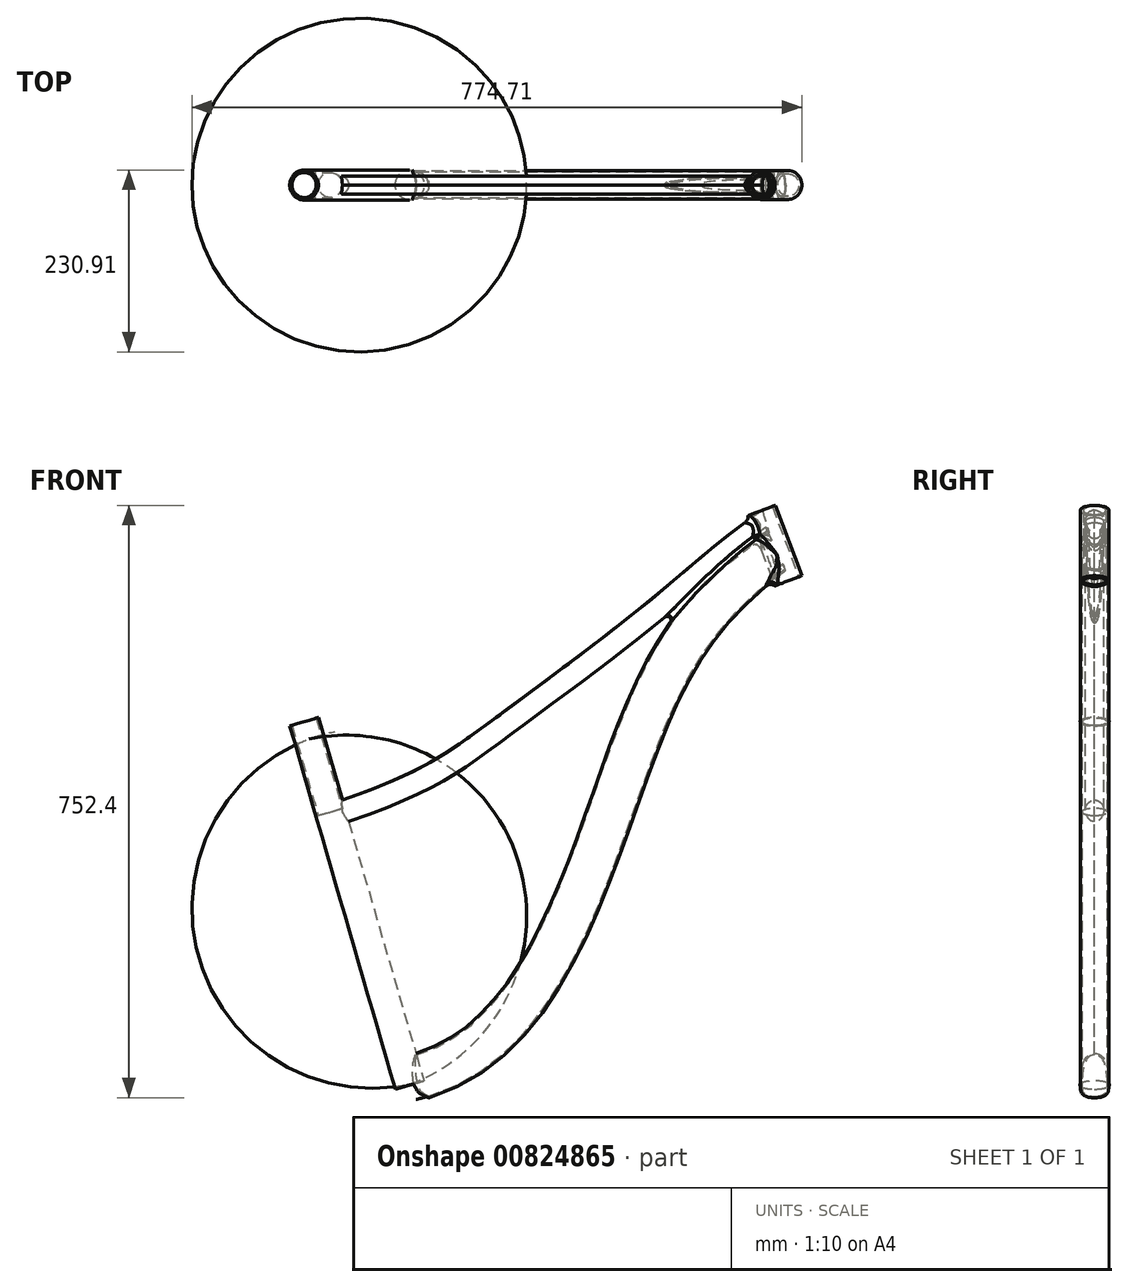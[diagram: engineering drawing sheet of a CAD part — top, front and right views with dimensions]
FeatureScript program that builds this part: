
annotation { "Feature Type Name" : "Feature", "Feature Type Description" : "" }
export const myFeature = defineFeature(function(context is Context, id is Id, definition is map)
    precondition{}
    {
        {
            var Q0;
            Q0=qCreatedBy(makeId("Front.planeOp"),FACE);
            var sketch = newSketch(context, id + "F0", { "sketchPlane" : qUnion([Q0])});
            skLineSegment(sketch, "E0", {"start": v(0, 0) * mm, "end": v(584, 0) * mm, "construction": true});
            skLineSegment(sketch, "E1", {"start": v(0, 0) * mm, "end": v(-584, 0) * mm, "construction": true});
            skCircle(sketch, "E2", {"center": v(-584, 0) * mm, "radius": 311 * mm});
            skCircle(sketch, "E3", {"center": v(584, 0) * mm, "radius": 311 * mm});
            skCircle(sketch, "E4", {"center": v(584, 0) * mm, "radius": 370 * mm});
            skCircle(sketch, "E5", {"center": v(-584, 0) * mm, "radius": 370 * mm});
            skLineSegment(sketch, "E6", {"start": v(-584, -70.94) * mm, "end": v(-139, -70.94) * mm, "construction": true});
            skLineSegment(sketch, "E7", {"start": v(-139, -70.94) * mm, "end": v(-139, 68.19) * mm, "construction": true});
            skLineSegment(sketch, "E8", {"start": v(584, 0) * mm, "end": v(308.44, 729.25) * mm, "construction": true});
            skLineSegment(sketch, "E9", {"start": v(-139, 0) * mm, "end": v(-321.56, 628.38) * mm, "construction": true});
            skPoint(sketch, "E10", {"position": v(-272.92, 460.94) * mm});
            skLineSegment(sketch, "E11", {"start": v(421.54, -332.43) * mm, "end": v(-746.46, -332.43) * mm, "construction": true});
            skPoint(sketch, "E12", {"position": v(329.44, 673.67) * mm});
            skFitSpline(sketch, "E13", {"points": [v(-139, 0) * mm, v(57.4, 180.26) * mm, v(171.31, 471.97) * mm, v(329.44, 673.67) * mm], "startDerivative": vector(868.1, 183) * mm, "endDerivative": vector(779.1, 577.52) * mm});
            skPoint(sketch, "E14", {"position": v(541.58, 112.25) * mm});
            skCircle(sketch, "E15", {"center": v(541.58, 112.25) * mm, "radius": 370 * mm, "construction": true});
            skCircle(sketch, "E16", {"center": v(541.58, 112.25) * mm, "radius": 311 * mm, "construction": true});
            skLineSegment(sketch, "E17", {"start": v(61.85, -332.43) * mm, "end": v(61.85, 447.57) * mm, "construction": true});
            skLineSegment(sketch, "E18", {"start": v(61.85, 447.57) * mm, "end": v(-37.41, 447.57) * mm, "construction": true});
            skFitSpline(sketch, "E19", {"points": [v(-239.4, 345.58) * mm, v(-37.41, 447.57) * mm, v(176.43, 610.15) * mm, v(312.12, 719.5) * mm], "startDerivative": vector(1021.83, 342.5) * mm, "endDerivative": vector(568.7, 395.8) * mm});
            skLineSegment(sketch, "E20", {"start": v(308.44, 729.25) * mm, "end": v(325.55, 735.72) * mm});
            skLineSegment(sketch, "E21", {"start": v(325.55, 735.72) * mm, "end": v(356.16, 654.7) * mm});
            skLineSegment(sketch, "E22", {"start": v(321.8, 734.3) * mm, "end": v(352.41, 653.3) * mm});
            skLineSegment(sketch, "E23", {"start": v(356.16, 654.7) * mm, "end": v(359.31, 646.35) * mm});
            skLineSegment(sketch, "E24", {"start": v(352.41, 653.3) * mm, "end": v(355.57, 644.94) * mm});
            skLineSegment(sketch, "E25", {"start": v(359.31, 646.35) * mm, "end": v(355.57, 644.94) * mm});
            skLineSegment(sketch, "E26", {"start": v(-272.92, 460.94) * mm, "end": v(-254.72, 466.23) * mm});
            skLineSegment(sketch, "E27", {"start": v(-254.72, 466.23) * mm, "end": v(-119.27, 0) * mm});
            skLineSegment(sketch, "E28", {"start": v(-257.6, 465.4) * mm, "end": v(-122.4, 0) * mm});
            skLineSegment(sketch, "E29", {"start": v(-139, 0) * mm, "end": v(-272.92, 460.94) * mm});
            skLineSegment(sketch, "E30", {"start": v(-139, 0) * mm, "end": v(-125.59, -46.16) * mm});
            skLineSegment(sketch, "E31", {"start": v(-119.27, 0) * mm, "end": v(-125.38, 21.03) * mm});
            skLineSegment(sketch, "E32", {"start": v(-125.38, 21.03) * mm, "end": v(-105.22, -48.34) * mm});
            skLineSegment(sketch, "E33", {"start": v(-105.22, -48.34) * mm, "end": v(-125.59, -46.16) * mm});
            skSolve(sketch);
        }
        {
            var Q0;
            Q0=qCreatedBy(makeId("Right.planeOp"),FACE);
            cPlane(context, id + "F1", {"entities" : qUnion([Q0]), "cplaneType" : CPlaneType.OFFSET, "offset" : 139 * mm, "oppositeDirection" : true, "width" : 150 * mm, "height" : 150 * mm});
        }
        {
            var Q0;
            Q0=qCreatedBy(id+"F1.planeOp",FACE);
            var sketch = newSketch(context, id + "F2", { "sketchPlane" : qUnion([Q0])});
            skLineSegment(sketch, "E34", {"start": v(0, 0) * mm, "end": v(0, -22.68) * mm});
            skFitSpline(sketch, "E35", {"points": [v(0, -22.68) * mm, v(-9.06, -21.02) * mm, v(-16.68, -13.33) * mm, v(-17.93, -5.33) * mm, v(-18.18, 0) * mm, v(-14.5, 25.97) * mm, v(-7.81, 34.98) * mm, v(0, 37.32) * mm], "startDerivative": vector(-73.75, 0) * mm, "endDerivative": vector(85.37, 4.1) * mm});
            skFitSpline(sketch, "E36.MirrorCS", {"points": [v(0, -22.68) * mm, v(9.06, -21.02) * mm, v(16.68, -13.33) * mm, v(17.93, -5.33) * mm, v(18.18, 0) * mm, v(14.5, 25.97) * mm, v(7.81, 34.98) * mm, v(0, 37.32) * mm], "startDerivative": vector(73.75, 0) * mm, "endDerivative": vector(-85.37, 4.1) * mm});
            skFitSpline(sketch, "E37.0", {"points": [v(0, -20.68) * mm, v(0.74, -20.68) * mm, v(2.17, -20.65) * mm, v(4.14, -20.47) * mm, v(5.67, -20.17) * mm, v(6.85, -19.8) * mm, v(7.73, -19.45) * mm, v(8.6, -19.02) * mm, v(9.78, -18.33) * mm, v(11.23, -17.27) * mm, v(12.54, -16) * mm, v(13.45, -14.9) * mm, v(14.05, -14.06) * mm, v(14.47, -13.33) * mm, v(14.75, -12.75) * mm, v(15, -12.18) * mm, v(15.26, -11.43) * mm, v(15.57, -10.2) * mm, v(15.74, -8.92) * mm, v(15.84, -7.66) * mm, v(15.88, -6.74) * mm, v(15.9, -6) * mm, v(15.93, -5.43) * mm, v(15.95, -4.87) * mm, v(16, -4.23) * mm, v(16.07, -3.29) * mm, v(16.13, -2.37) * mm, v(16.18, -1.27) * mm, v(16.19, -0.29) * mm, v(16.17, 0.91) * mm, v(16.12, 2.77) * mm, v(15.97, 5.52) * mm, v(15.67, 9.28) * mm, v(15.22, 13.27) * mm, v(14.61, 17.3) * mm, v(13.98, 20.48) * mm, v(13.4, 22.83) * mm, v(12.91, 24.45) * mm, v(12.4, 25.9) * mm, v(11.67, 27.62) * mm, v(10.68, 29.4) * mm, v(9.63, 30.77) * mm, v(8.75, 31.7) * mm, v(8.08, 32.3) * mm, v(7.51, 32.75) * mm, v(7.05, 33.09) * mm, v(6.7, 33.32) * mm, v(6.35, 33.55) * mm, v(5.9, 33.82) * mm, v(5.32, 34.13) * mm, v(4.61, 34.45) * mm, v(3.61, 34.8) * mm, v(2.18, 35.14) * mm, v(0.73, 35.28) * mm, v(-0.1, 35.32) * mm]});
            skFitSpline(sketch, "E37.1", {"points": [v(0, -20.68) * mm, v(-0.74, -20.68) * mm, v(-2.17, -20.65) * mm, v(-4.14, -20.47) * mm, v(-5.67, -20.17) * mm, v(-6.85, -19.8) * mm, v(-7.73, -19.45) * mm, v(-8.6, -19.02) * mm, v(-9.78, -18.33) * mm, v(-11.23, -17.27) * mm, v(-12.54, -16) * mm, v(-13.45, -14.9) * mm, v(-14.05, -14.06) * mm, v(-14.47, -13.33) * mm, v(-14.75, -12.75) * mm, v(-15, -12.18) * mm, v(-15.26, -11.43) * mm, v(-15.57, -10.2) * mm, v(-15.74, -8.92) * mm, v(-15.84, -7.66) * mm, v(-15.88, -6.74) * mm, v(-15.9, -6) * mm, v(-15.93, -5.43) * mm, v(-15.95, -4.87) * mm, v(-16, -4.23) * mm, v(-16.07, -3.29) * mm, v(-16.13, -2.37) * mm, v(-16.18, -1.27) * mm, v(-16.19, -0.29) * mm, v(-16.17, 0.91) * mm, v(-16.12, 2.77) * mm, v(-15.97, 5.52) * mm, v(-15.67, 9.28) * mm, v(-15.22, 13.27) * mm, v(-14.61, 17.3) * mm, v(-13.98, 20.48) * mm, v(-13.4, 22.83) * mm, v(-12.91, 24.45) * mm, v(-12.4, 25.9) * mm, v(-11.67, 27.62) * mm, v(-10.68, 29.4) * mm, v(-9.63, 30.77) * mm, v(-8.75, 31.7) * mm, v(-8.08, 32.3) * mm, v(-7.51, 32.75) * mm, v(-7.05, 33.09) * mm, v(-6.7, 33.32) * mm, v(-6.35, 33.55) * mm, v(-5.9, 33.82) * mm, v(-5.32, 34.13) * mm, v(-4.61, 34.45) * mm, v(-3.61, 34.8) * mm, v(-2.18, 35.14) * mm, v(-0.73, 35.28) * mm, v(0.1, 35.32) * mm]});
            skSolve(sketch);
        }
        {
            var Q0;
            Q0=qCreatedBy(makeId("Right.planeOp"),FACE);
            cPlane(context, id + "F3", {"entities" : qUnion([Q0]), "cplaneType" : CPlaneType.OFFSET, "offset" : 239.4 * mm, "oppositeDirection" : true, "width" : 150 * mm, "height" : 150 * mm});
        }
        {
            var Q0;
            Q0=qCreatedBy(id+"F3.planeOp",FACE);
            var sketch = newSketch(context, id + "F4", { "sketchPlane" : qUnion([Q0])});
            skLineSegment(sketch, "E38", {"start": v(0, 345.64) * mm, "end": v(0, 356.28) * mm});
            skFitSpline(sketch, "E39", {"points": [v(0, 356.28) * mm, v(-8.58, 352.29) * mm, v(-11.34, 340.53) * mm, v(-5.74, 328.42) * mm, v(0, 326.28) * mm], "startDerivative": vector(-28.44, 1.13) * mm, "endDerivative": vector(40.47, -0.68) * mm});
            skFitSpline(sketch, "E40.MirrorCS", {"points": [v(0, 356.28) * mm, v(8.58, 352.29) * mm, v(11.34, 340.53) * mm, v(5.74, 328.42) * mm, v(0, 326.28) * mm], "startDerivative": vector(28.44, 1.13) * mm, "endDerivative": vector(-40.47, -0.68) * mm});
            skFitSpline(sketch, "E41.0", {"points": [v(-0.08, 354.28) * mm, v(-0.25, 354.29) * mm, v(-0.7, 354.27) * mm, v(-1.85, 354.07) * mm, v(-3.23, 353.6) * mm, v(-4.61, 352.9) * mm, v(-5.61, 352.26) * mm, v(-6.37, 351.66) * mm, v(-6.92, 351.14) * mm, v(-7.42, 350.6) * mm, v(-7.96, 349.88) * mm, v(-8.51, 348.93) * mm, v(-8.95, 347.88) * mm, v(-9.4, 346.38) * mm, v(-9.67, 344.32) * mm, v(-9.57, 342.07) * mm, v(-9.27, 340.2) * mm, v(-8.82, 338.3) * mm, v(-8.03, 335.94) * mm, v(-6.8, 333.31) * mm, v(-5.67, 331.47) * mm, v(-4.78, 330.3) * mm, v(-4.15, 329.63) * mm, v(-3.6, 329.15) * mm, v(-3.08, 328.83) * mm, v(-2.54, 328.6) * mm, v(-1.88, 328.43) * mm, v(-1.05, 328.32) * mm, v(-0.35, 328.28) * mm, v(0.03, 328.28) * mm]});
            skFitSpline(sketch, "E42.0", {"points": [v(0.08, 354.28) * mm, v(0.25, 354.29) * mm, v(0.7, 354.27) * mm, v(1.85, 354.07) * mm, v(3.23, 353.6) * mm, v(4.61, 352.9) * mm, v(5.61, 352.26) * mm, v(6.37, 351.66) * mm, v(6.92, 351.14) * mm, v(7.42, 350.6) * mm, v(7.96, 349.88) * mm, v(8.51, 348.93) * mm, v(8.95, 347.88) * mm, v(9.4, 346.38) * mm, v(9.67, 344.32) * mm, v(9.57, 342.07) * mm, v(9.27, 340.2) * mm, v(8.82, 338.3) * mm, v(8.03, 335.94) * mm, v(6.8, 333.31) * mm, v(5.67, 331.47) * mm, v(4.78, 330.3) * mm, v(4.15, 329.63) * mm, v(3.6, 329.15) * mm, v(3.08, 328.83) * mm, v(2.54, 328.6) * mm, v(1.88, 328.43) * mm, v(1.05, 328.32) * mm, v(0.35, 328.28) * mm, v(-0.03, 328.28) * mm]});
            skLineSegment(sketch, "E43", {"start": v(-0.57, 354.26) * mm, "end": v(0.57, 354.26) * mm});
            skLineSegment(sketch, "E44", {"start": v(0, 356.28) * mm, "end": v(0, 343.94) * mm});
            skSolve(sketch);
        }
        {
            var Q0;
            Q0=makeQuery(id+"F4.imprint","IMPRINT",FACE,{"disambiguationData":[TD([[makeQuery(id+"F4.imprint","IMPRINT",EDGE,{"derivedFrom":sQuery(id+"F4.wireOp",EDGE,"E39")}),1.0]])]});
            var Q1;
            Q1=sQuery(id+"F0.wireOp",EDGE,"E19");
            sweep(context, id + "F5", {"profiles" : qUnion([Q0]), "path" : qUnion([Q1])});
        }
        {
            var Q0;
            Q0=makeQuery(id+"F2.imprint","IMPRINT",FACE,{"disambiguationData":[TD([[makeQuery(id+"F2.imprint","IMPRINT",EDGE,{"derivedFrom":sQuery(id+"F2.wireOp",EDGE,"E35")}),-1.0]])]});
            var Q1;
            Q1=sQuery(id+"F0.wireOp",EDGE,"E13");
            sweep(context, id + "F6", {"profiles" : qUnion([Q0]), "path" : qUnion([Q1])});
        }
        {
            var Q0;
            {var subQ1=sQuery(id+"F0.wireOp",EDGE,"E21");Q0=makeQuery(id+"F0.imprint","IMPRINT",FACE,{"disambiguationData":[TD([[makeQuery(id+"F0.imprint","IMPRINT",EDGE,{"derivedFrom":subQ1}),-1.0]])]});}
            var Q1;
            Q1=sQuery(id+"F0.wireOp",EDGE,"E8");
            revolve(context, id + "F7", {"operationType" : NewBodyOperationType.ADD, "surfaceOperationType" : NewSurfaceOperationType.NEW, "entities" : qUnion([Q0]), "axis" : qUnion([Q1]), "revolveType" : RevolveType.FULL});
        }
        {
            var Q0;
            Q0=makeQuery(id+"F7.boolean.opBoolean","INTERSECT",EDGE,{"disambiguationData":[OD(0.0)],"derivedFrom":[makeQuery(id+"F5.opSweep","SWEPT_FACE",FACE,{"disambiguationData":[OSD([sQuery(id+"F0.wireOp",EDGE,"E19"),sQuery(id+"F4.wireOp",EDGE,"E39")])]}),makeQuery(id+"F6.opSweep","SWEPT_FACE",FACE,{"disambiguationData":[OSD([sQuery(id+"F0.wireOp",EDGE,"E13"),sQuery(id+"F2.wireOp",EDGE,"E35")])]})]});
            var Q1;
            Q1=makeQuery(id+"F7.boolean.opBoolean","INTERSECT",EDGE,{"disambiguationData":[OD(0.0)],"derivedFrom":[makeQuery(id+"F5.opSweep","SWEPT_FACE",FACE,{"disambiguationData":[OSD([sQuery(id+"F0.wireOp",EDGE,"E19"),sQuery(id+"F4.wireOp",EDGE,"E40.MirrorCS")])]}),makeQuery(id+"F6.opSweep","SWEPT_FACE",FACE,{"disambiguationData":[OSD([sQuery(id+"F0.wireOp",EDGE,"E13"),sQuery(id+"F2.wireOp",EDGE,"E36.MirrorCS")])]})]});
            fillet(context, id + "F8", {"entities" : qUnion([Q0, Q1]), "radius" : 5 * mm, "tangentPropagation" : true, "allowEdgeOverflow" : false});
        }
        {
            var Q0;
            Q0=makeQuery(id+"F7.boolean.opBoolean","INTERSECT",EDGE,{"disambiguationData":[OD(1.0)],"derivedFrom":[makeQuery(id+"F5.opSweep","SWEPT_FACE",FACE,{"disambiguationData":[OSD([sQuery(id+"F0.wireOp",EDGE,"E19"),sQuery(id+"F4.wireOp",EDGE,"E39")])]}),makeQuery(id+"F7.opRevolve","SWEPT_FACE",FACE,{"disambiguationData":[OSD([sQuery(id+"F0.wireOp",EDGE,"E21"),sQuery(id+"F0.wireOp",EDGE,"E23")])]})]});
            var Q1;
            Q1=makeQuery(id+"F7.boolean.opBoolean","INTERSECT",EDGE,{"disambiguationData":[OD(0.0)],"derivedFrom":[makeQuery(id+"F6.opSweep","SWEPT_FACE",FACE,{"disambiguationData":[OSD([sQuery(id+"F0.wireOp",EDGE,"E13"),sQuery(id+"F2.wireOp",EDGE,"E35")])]}),makeQuery(id+"F7.opRevolve","SWEPT_FACE",FACE,{"disambiguationData":[OSD([sQuery(id+"F0.wireOp",EDGE,"E21"),sQuery(id+"F0.wireOp",EDGE,"E23")])]})]});
            var Q2;
            {var subQ0=sQuery(id+"F0.wireOp",EDGE,"E13");var subQ1=makeQuery(id+"F6.opSweep","SWEPT_FACE",FACE,{"disambiguationData":[OSD([subQ0,sQuery(id+"F2.wireOp",EDGE,"E35")])]});var subQ2=sQuery(id+"F0.wireOp",EDGE,"E19");var subQ3=makeQuery(id+"F5.opSweep","SWEPT_FACE",FACE,{"disambiguationData":[OSD([subQ2,sQuery(id+"F4.wireOp",EDGE,"E39")])]});Q2=makeQuery(id+"F8.opFillet","BLEND_EDGE",EDGE,{"blendedFrom":[makeQuery(id+"F7.boolean.opBoolean","INTERSECT",EDGE,{"disambiguationData":[OD(0.0)],"derivedFrom":[subQ3,subQ1]}),makeQuery(id+"F7.boolean.opBoolean","SPLIT",FACE,{"disambiguationData":[TD([makeQuery(id+"F7.opRevolve","SWEPT_FACE",FACE,{"disambiguationData":[OSD([sQuery(id+"F0.wireOp",EDGE,"E20")])]})])],"derivedFrom":makeQuery(id+"F7.opRevolve","SWEPT_FACE",FACE,{"disambiguationData":[OSD([sQuery(id+"F0.wireOp",EDGE,"E21"),sQuery(id+"F0.wireOp",EDGE,"E23")])]})})],"blendedInto":[makeQuery(id+"F7.boolean.opBoolean","SPLIT",FACE,{"disambiguationData":[TD([makeQuery(id+"F7.opRevolve","SWEPT_FACE",FACE,{"disambiguationData":[OSD([sQuery(id+"F0.wireOp",EDGE,"E20")])]})])],"derivedFrom":makeQuery(id+"F7.opRevolve","SWEPT_FACE",FACE,{"disambiguationData":[OSD([sQuery(id+"F0.wireOp",EDGE,"E21"),sQuery(id+"F0.wireOp",EDGE,"E23")])]})})]});}
            var Q3;
            Q3=makeQuery(id+"F7.boolean.opBoolean","INTERSECT",EDGE,{"disambiguationData":[OD(0.0)],"derivedFrom":[makeQuery(id+"F6.opSweep","SWEPT_FACE",FACE,{"disambiguationData":[OSD([sQuery(id+"F0.wireOp",EDGE,"E13"),sQuery(id+"F2.wireOp",EDGE,"E36.MirrorCS")])]}),makeQuery(id+"F7.opRevolve","SWEPT_FACE",FACE,{"disambiguationData":[OSD([sQuery(id+"F0.wireOp",EDGE,"E21"),sQuery(id+"F0.wireOp",EDGE,"E23")])]})]});
            var Q4;
            Q4=makeQuery(id+"F7.boolean.opBoolean","INTERSECT",EDGE,{"disambiguationData":[OD(1.0)],"derivedFrom":[makeQuery(id+"F5.opSweep","SWEPT_FACE",FACE,{"disambiguationData":[OSD([sQuery(id+"F0.wireOp",EDGE,"E19"),sQuery(id+"F4.wireOp",EDGE,"E40.MirrorCS")])]}),makeQuery(id+"F7.opRevolve","SWEPT_FACE",FACE,{"disambiguationData":[OSD([sQuery(id+"F0.wireOp",EDGE,"E21"),sQuery(id+"F0.wireOp",EDGE,"E23")])]})]});
            var Q5;
            {var subQ0=sQuery(id+"F0.wireOp",EDGE,"E13");var subQ1=makeQuery(id+"F6.opSweep","SWEPT_FACE",FACE,{"disambiguationData":[OSD([subQ0,sQuery(id+"F2.wireOp",EDGE,"E36.MirrorCS")])]});var subQ2=sQuery(id+"F0.wireOp",EDGE,"E19");var subQ3=makeQuery(id+"F5.opSweep","SWEPT_FACE",FACE,{"disambiguationData":[OSD([subQ2,sQuery(id+"F4.wireOp",EDGE,"E40.MirrorCS")])]});Q5=makeQuery(id+"F8.opFillet","BLEND_EDGE",EDGE,{"blendedFrom":[makeQuery(id+"F7.boolean.opBoolean","INTERSECT",EDGE,{"disambiguationData":[OD(0.0)],"derivedFrom":[subQ3,subQ1]}),makeQuery(id+"F7.boolean.opBoolean","SPLIT",FACE,{"disambiguationData":[TD([makeQuery(id+"F7.opRevolve","SWEPT_FACE",FACE,{"disambiguationData":[OSD([sQuery(id+"F0.wireOp",EDGE,"E20")])]})])],"derivedFrom":makeQuery(id+"F7.opRevolve","SWEPT_FACE",FACE,{"disambiguationData":[OSD([sQuery(id+"F0.wireOp",EDGE,"E21"),sQuery(id+"F0.wireOp",EDGE,"E23")])]})})],"blendedInto":[makeQuery(id+"F7.boolean.opBoolean","SPLIT",FACE,{"disambiguationData":[TD([makeQuery(id+"F7.opRevolve","SWEPT_FACE",FACE,{"disambiguationData":[OSD([sQuery(id+"F0.wireOp",EDGE,"E20")])]})])],"derivedFrom":makeQuery(id+"F7.opRevolve","SWEPT_FACE",FACE,{"disambiguationData":[OSD([sQuery(id+"F0.wireOp",EDGE,"E21"),sQuery(id+"F0.wireOp",EDGE,"E23")])]})})]});}
            var Q6;
            Q6=makeQuery(id+"F7.boolean.opBoolean","INTERSECT",EDGE,{"disambiguationData":[OD(0.0)],"derivedFrom":[makeQuery(id+"F5.opSweep","SWEPT_FACE",FACE,{"disambiguationData":[OSD([sQuery(id+"F0.wireOp",EDGE,"E19"),sQuery(id+"F4.wireOp",EDGE,"E39")])]}),makeQuery(id+"F7.opRevolve","SWEPT_FACE",FACE,{"disambiguationData":[OSD([sQuery(id+"F0.wireOp",EDGE,"E21"),sQuery(id+"F0.wireOp",EDGE,"E23")])]})]});
            var Q7;
            Q7=makeQuery(id+"F7.boolean.opBoolean","INTERSECT",EDGE,{"disambiguationData":[OD(0.0)],"derivedFrom":[makeQuery(id+"F5.opSweep","SWEPT_FACE",FACE,{"disambiguationData":[OSD([sQuery(id+"F0.wireOp",EDGE,"E19"),sQuery(id+"F4.wireOp",EDGE,"E40.MirrorCS")])]}),makeQuery(id+"F7.opRevolve","SWEPT_FACE",FACE,{"disambiguationData":[OSD([sQuery(id+"F0.wireOp",EDGE,"E21"),sQuery(id+"F0.wireOp",EDGE,"E23")])]})]});
            fillet(context, id + "F9", {"entities" : qUnion([Q0, Q1, Q2, Q3, Q4, Q5, Q6, Q7]), "radius" : 10 * mm, "rho" : 0.5, "crossSection" : FilletCrossSection.CONIC, "allowEdgeOverflow" : false});
        }
        {
            var Q0;
            {var subQ0=sQuery(id+"F0.wireOp",EDGE,"E27");var subQ1=sQuery(id+"F0.wireOp",EDGE,"E19");var subQ2=makeQuery(id+"F0.imprint","INTERSECT",VERTEX,{"derivedFrom":[subQ1,subQ0]});Q0=makeQuery(id+"F0.imprint","IMPRINT",FACE,{"disambiguationData":[TD([[makeQuery(id+"F0.imprint","IMPRINT",EDGE,{"disambiguationData":[TD([[subQ2,1.0]])],"derivedFrom":subQ1}),1.0]])]});}
            var Q1;
            {var subQ0=sQuery(id+"F0.wireOp",EDGE,"E29");var subQ1=sQuery(id+"F0.wireOp",EDGE,"E19");var subQ2=makeQuery(id+"F0.imprint","INTERSECT",VERTEX,{"derivedFrom":[subQ1,subQ0]});Q1=makeQuery(id+"F0.imprint","IMPRINT",FACE,{"disambiguationData":[TD([[makeQuery(id+"F0.imprint","IMPRINT",EDGE,{"disambiguationData":[TD([[subQ2,-1.0]])],"derivedFrom":subQ1}),1.0]])]});}
            var Q2;
            {var subQ0=sQuery(id+"F0.wireOp",EDGE,"E29");var subQ1=sQuery(id+"F0.wireOp",EDGE,"E13");var subQ2=makeQuery(id+"F0.imprint","INTERSECT",VERTEX,{"derivedFrom":[subQ1,subQ0]});Q2=makeQuery(id+"F0.imprint","IMPRINT",FACE,{"disambiguationData":[TD([[makeQuery(id+"F0.imprint","IMPRINT",EDGE,{"disambiguationData":[TD([[subQ2,-1.0]])],"derivedFrom":subQ1}),1.0]])]});}
            var Q3;
            {var subQ0=sQuery(id+"F0.wireOp",EDGE,"E27");var subQ1=sQuery(id+"F0.wireOp",EDGE,"E13");var subQ2=makeQuery(id+"F0.imprint","INTERSECT",VERTEX,{"derivedFrom":[subQ1,subQ0]});Q3=makeQuery(id+"F0.imprint","IMPRINT",FACE,{"disambiguationData":[TD([[makeQuery(id+"F0.imprint","IMPRINT",EDGE,{"disambiguationData":[TD([[subQ2,1.0]])],"derivedFrom":subQ1}),1.0]])]});}
            var Q4;
            {var subQ0=sQuery(id+"F0.wireOp",EDGE,"E30");Q4=makeQuery(id+"F0.imprint","IMPRINT",FACE,{"disambiguationData":[TD([[makeQuery(id+"F0.imprint","IMPRINT",EDGE,{"derivedFrom":subQ0}),1.0]])]});}
            var Q5;
            {var subQ1=sQuery(id+"F0.wireOp",EDGE,"E13");var subQ5=sQuery(id+"F0.wireOp",EDGE,"E32");var subQ9=makeQuery(id+"F0.imprint","INTERSECT",VERTEX,{"derivedFrom":[subQ1,subQ5]});Q5=makeQuery(id+"F0.imprint","IMPRINT",FACE,{"disambiguationData":[TD([[makeQuery(id+"F0.imprint","IMPRINT",EDGE,{"disambiguationData":[TD([[subQ9,1.0]])],"derivedFrom":subQ1}),1.0]])]});}
            var Q6;
            Q6=sQuery(id+"F0.wireOp",EDGE,"E29");
            revolve(context, id + "F10", {"operationType" : NewBodyOperationType.REMOVE, "surfaceOperationType" : NewSurfaceOperationType.NEW, "entities" : qUnion([Q0, Q1, Q2, Q3, Q4, Q5]), "axis" : qUnion([Q6]), "revolveType" : RevolveType.FULL, "oppositeDirection" : true});
        }
        {
            var Q0;
            {var subQ1=sQuery(id+"F0.wireOp",EDGE,"E13");var subQ5=sQuery(id+"F0.wireOp",EDGE,"E32");var subQ9=makeQuery(id+"F0.imprint","INTERSECT",VERTEX,{"derivedFrom":[subQ1,subQ5]});Q0=makeQuery(id+"F0.imprint","IMPRINT",FACE,{"disambiguationData":[TD([[makeQuery(id+"F0.imprint","IMPRINT",EDGE,{"disambiguationData":[TD([[subQ9,1.0]])],"derivedFrom":subQ1}),1.0]])]});}
            var Q1;
            {var subQ0=sQuery(id+"F0.wireOp",EDGE,"E27");var subQ1=sQuery(id+"F0.wireOp",EDGE,"E19");var subQ2=makeQuery(id+"F0.imprint","INTERSECT",VERTEX,{"derivedFrom":[subQ1,subQ0]});Q1=makeQuery(id+"F0.imprint","IMPRINT",FACE,{"disambiguationData":[TD([[makeQuery(id+"F0.imprint","IMPRINT",EDGE,{"disambiguationData":[TD([[subQ2,1.0]])],"derivedFrom":subQ1}),1.0]])]});}
            var Q2;
            Q2=sQuery(id+"F0.wireOp",EDGE,"E29");
            revolve(context, id + "F11", {"operationType" : NewBodyOperationType.ADD, "surfaceOperationType" : NewSurfaceOperationType.NEW, "entities" : qUnion([Q0, Q1]), "axis" : qUnion([Q2]), "revolveType" : RevolveType.FULL});
        }
    });
